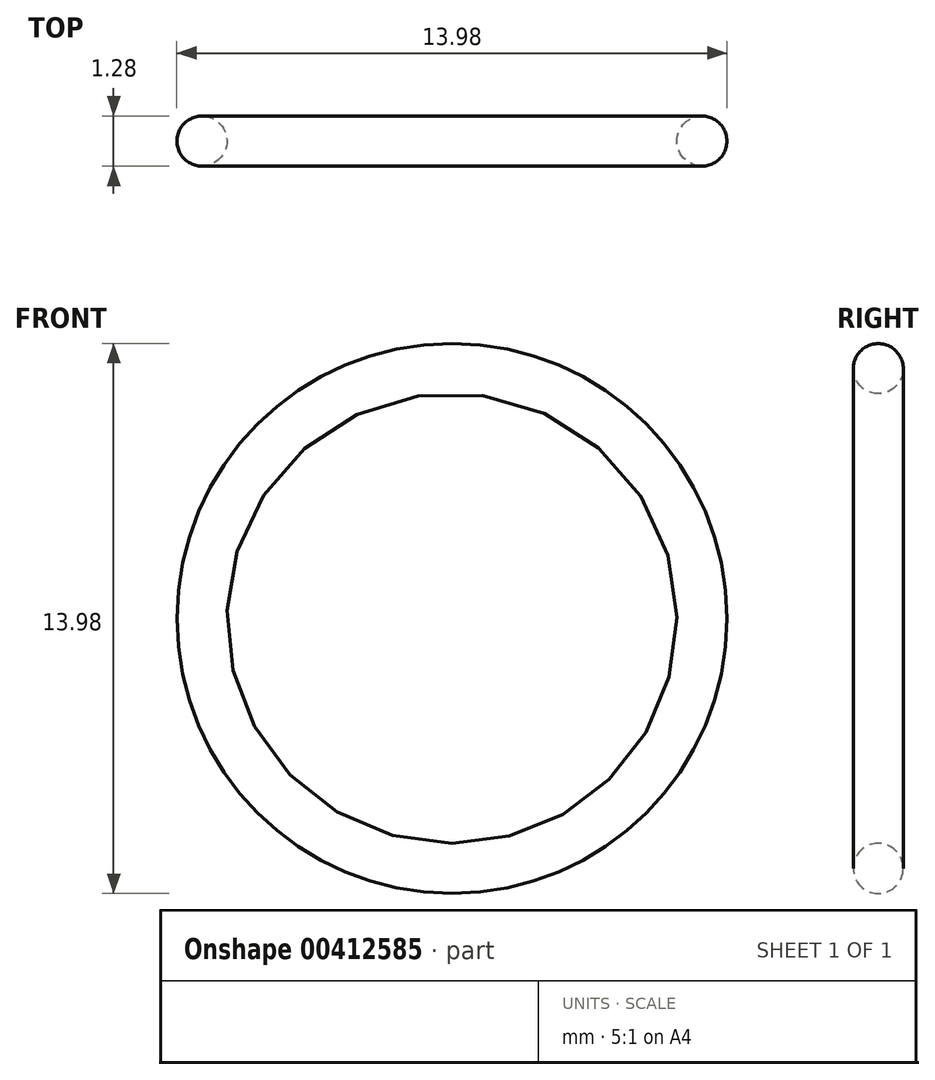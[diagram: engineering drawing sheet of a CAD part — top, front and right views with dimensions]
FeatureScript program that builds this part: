
annotation { "Feature Type Name" : "Feature", "Feature Type Description" : "" }
export const myFeature = defineFeature(function(context is Context, id is Id, definition is map)
    precondition{}
    {
        {
            var Q0;
            Q0=qCreatedBy(makeId("Front.planeOp"),FACE);
            var sketch = newSketch(context, id + "F0", { "sketchPlane" : qUnion([Q0])});
            skCircle(sketch, "E0", {"center": v(0, 0) * mm, "radius": 6.35 * mm});
            skSolve(sketch);
        }
        {
            var Q0;
            Q0=qCreatedBy(makeId("Right.planeOp"),FACE);
            var sketch = newSketch(context, id + "F1", { "sketchPlane" : qUnion([Q0])});
            skLineSegment(sketch, "E1.0", {"start": v(0, -6.35) * mm, "end": v(0, 6.35) * mm});
            skCircle(sketch, "E2", {"center": v(0, 6.35) * mm, "radius": 0.64 * mm});
            skSolve(sketch);
        }
        {
            var Q0;
            Q0=qSketchRegion(id+"F1",true);
            var Q1;
            Q1=sQuery(id+"F0.wireOp",EDGE,"E0");
            sweep(context, id + "F2", {"profiles" : qUnion([Q0]), "path" : qUnion([Q1])});
        }
    });
